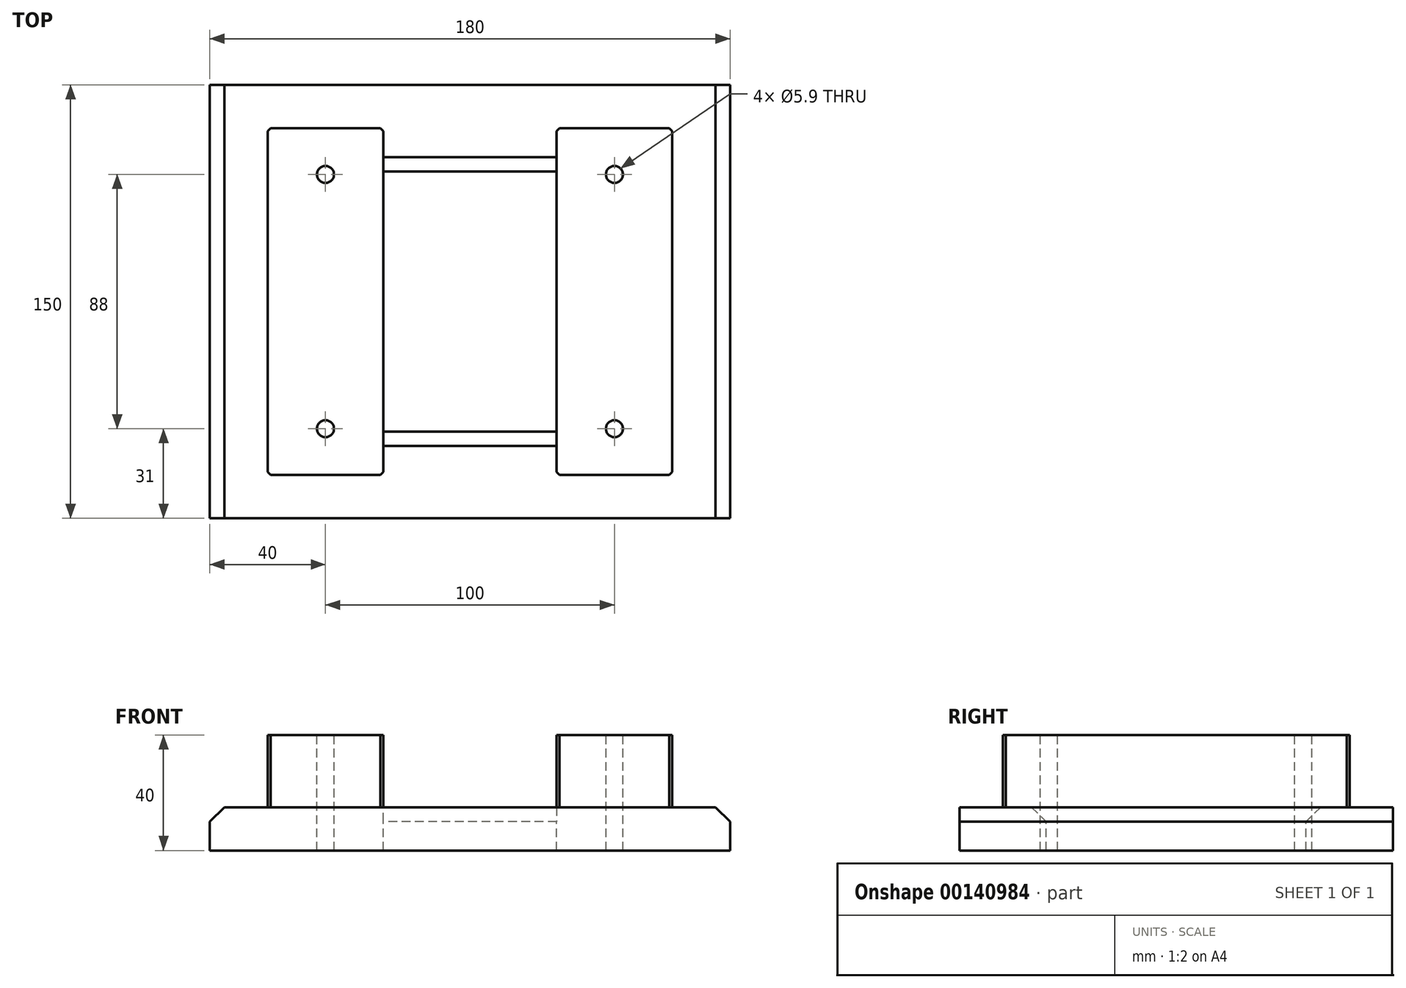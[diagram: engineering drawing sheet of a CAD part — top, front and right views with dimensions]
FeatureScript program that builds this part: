
annotation { "Feature Type Name" : "Feature", "Feature Type Description" : "" }
export const myFeature = defineFeature(function(context is Context, id is Id, definition is map)
    precondition{}
    {
        {
            var Q0;
            Q0=qCreatedBy(makeId("Top.planeOp"),FACE);
            var sketch = newSketch(context, id + "F0", { "sketchPlane" : qUnion([Q0])});
            skLineSegment(sketch, "E0.bottom", {"start": v(90, 75) * mm, "end": v(-90, 75) * mm});
            skLineSegment(sketch, "E0.top", {"start": v(90, -75) * mm, "end": v(-90, -75) * mm});
            skLineSegment(sketch, "E0.left", {"start": v(90, 75) * mm, "end": v(90, -75) * mm});
            skLineSegment(sketch, "E0.right", {"start": v(-90, 75) * mm, "end": v(-90, -75) * mm});
            skPoint(sketch, "E0.middle", {"position": v(0, 0) * mm});
            skLineSegment(sketch, "E1.bottom", {"start": v(30, 45) * mm, "end": v(-30, 45) * mm});
            skLineSegment(sketch, "E1.top", {"start": v(30, -45) * mm, "end": v(-30, -45) * mm});
            skLineSegment(sketch, "E1.left", {"start": v(30, 45) * mm, "end": v(30, -45) * mm});
            skLineSegment(sketch, "E1.right", {"start": v(-30, 45) * mm, "end": v(-30, -45) * mm});
            skLineSegment(sketch, "E2.bottom", {"start": v(50, 44) * mm, "end": v(-50, 44) * mm, "construction": true});
            skLineSegment(sketch, "E2.top", {"start": v(50, -44) * mm, "end": v(-50, -44) * mm, "construction": true});
            skLineSegment(sketch, "E2.left", {"start": v(50, 44) * mm, "end": v(50, -44) * mm, "construction": true});
            skLineSegment(sketch, "E2.right", {"start": v(-50, 44) * mm, "end": v(-50, -44) * mm, "construction": true});
            skCircle(sketch, "E3", {"center": v(-50, 44) * mm, "radius": 2.95 * mm});
            skCircle(sketch, "E4", {"center": v(50, 44) * mm, "radius": 2.95 * mm});
            skCircle(sketch, "E5", {"center": v(50, -44) * mm, "radius": 2.95 * mm});
            skCircle(sketch, "E6", {"center": v(-50, -44) * mm, "radius": 2.95 * mm});
            skLineSegment(sketch, "E7.bottom", {"start": v(-30, 60) * mm, "end": v(-70, 60) * mm});
            skLineSegment(sketch, "E7.top", {"start": v(-30, -60) * mm, "end": v(-70, -60) * mm});
            skLineSegment(sketch, "E7.left", {"start": v(-30, 60) * mm, "end": v(-30, -60) * mm});
            skLineSegment(sketch, "E7.right", {"start": v(-70, 60) * mm, "end": v(-70, -60) * mm});
            skPoint(sketch, "E7.middle", {"position": v(-50, 0) * mm});
            skLineSegment(sketch, "E8.bottom", {"start": v(70, 60) * mm, "end": v(30, 60) * mm});
            skLineSegment(sketch, "E8.top", {"start": v(70, -60) * mm, "end": v(30, -60) * mm});
            skLineSegment(sketch, "E8.left", {"start": v(70, 60) * mm, "end": v(70, -60) * mm});
            skLineSegment(sketch, "E8.right", {"start": v(30, 60) * mm, "end": v(30, -60) * mm});
            skPoint(sketch, "E8.middle", {"position": v(50, 0) * mm});
            skSolve(sketch);
        }
        {
            var Q0;
            Q0=makeQuery(id+"F0.imprint","IMPRINT",FACE,{"disambiguationData":[TD([[makeQuery(id+"F0.imprint","IMPRINT",EDGE,{"derivedFrom":sQuery(id+"F0.wireOp",EDGE,"E0.bottom")}),1.0]])]});
            var Q1;
            Q1=makeQuery(id+"F0.imprint","IMPRINT",FACE,{"disambiguationData":[TD([[makeQuery(id+"F0.imprint","IMPRINT",EDGE,{"derivedFrom":sQuery(id+"F0.wireOp",EDGE,"E3")}),-1.0]])]});
            var Q2;
            Q2=makeQuery(id+"F0.imprint","IMPRINT",FACE,{"disambiguationData":[TD([[makeQuery(id+"F0.imprint","IMPRINT",EDGE,{"derivedFrom":sQuery(id+"F0.wireOp",EDGE,"E4")}),-1.0]])]});
            extrude(context, id + "F1", {"entities" : qUnion([Q0, Q1, Q2]), "oppositeDirection" : true, "depth" : 15 * mm});
        }
        {
            var Q0;
            Q0=makeQuery(id+"F0.imprint","IMPRINT",FACE,{"disambiguationData":[TD([[makeQuery(id+"F0.imprint","IMPRINT",EDGE,{"derivedFrom":sQuery(id+"F0.wireOp",EDGE,"E3")}),-1.0]])]});
            var Q1;
            Q1=makeQuery(id+"F0.imprint","IMPRINT",FACE,{"disambiguationData":[TD([[makeQuery(id+"F0.imprint","IMPRINT",EDGE,{"derivedFrom":sQuery(id+"F0.wireOp",EDGE,"E4")}),-1.0]])]});
            extrude(context, id + "F2", {"entities" : qUnion([Q0, Q1]), "operationType" : NewBodyOperationType.ADD, "depth" : 25 * mm});
        }
        {
            var Q0;
            Q0=makeQuery(id+"F2.opExtrude","SWEPT_EDGE",EDGE,{"disambiguationData":[OSD([sQuery(id+"F0.wireOp",EDGE,"E7.top"),sQuery(id+"F0.wireOp",EDGE,"E7.right")])]});
            var Q1;
            Q1=makeQuery(id+"F2.opExtrude","SWEPT_EDGE",EDGE,{"disambiguationData":[OSD([sQuery(id+"F0.wireOp",EDGE,"E7.top"),sQuery(id+"F0.wireOp",EDGE,"E7.left")])]});
            var Q2;
            Q2=makeQuery(id+"F2.opExtrude","SWEPT_EDGE",EDGE,{"disambiguationData":[OSD([sQuery(id+"F0.wireOp",EDGE,"E8.top"),sQuery(id+"F0.wireOp",EDGE,"E8.right")])]});
            var Q3;
            Q3=makeQuery(id+"F2.opExtrude","SWEPT_EDGE",EDGE,{"disambiguationData":[OSD([sQuery(id+"F0.wireOp",EDGE,"E8.top"),sQuery(id+"F0.wireOp",EDGE,"E8.left")])]});
            var Q4;
            Q4=makeQuery(id+"F2.opExtrude","SWEPT_EDGE",EDGE,{"disambiguationData":[OSD([sQuery(id+"F0.wireOp",EDGE,"E8.bottom"),sQuery(id+"F0.wireOp",EDGE,"E8.left")])]});
            var Q5;
            Q5=makeQuery(id+"F2.opExtrude","SWEPT_EDGE",EDGE,{"disambiguationData":[OSD([sQuery(id+"F0.wireOp",EDGE,"E8.bottom"),sQuery(id+"F0.wireOp",EDGE,"E8.right")])]});
            var Q6;
            Q6=makeQuery(id+"F2.opExtrude","SWEPT_EDGE",EDGE,{"disambiguationData":[OSD([sQuery(id+"F0.wireOp",EDGE,"E7.bottom"),sQuery(id+"F0.wireOp",EDGE,"E7.left")])]});
            var Q7;
            Q7=makeQuery(id+"F2.opExtrude","SWEPT_EDGE",EDGE,{"disambiguationData":[OSD([sQuery(id+"F0.wireOp",EDGE,"E7.bottom"),sQuery(id+"F0.wireOp",EDGE,"E7.right")])]});
            chamfer(context, id + "F3", {"entities" : qUnion([Q0, Q1, Q2, Q3, Q4, Q5, Q6, Q7]), "width" : 1 * mm, "tangentPropagation" : true});
        }
        {
            var Q0;
            Q0=makeQuery(id+"F1.opExtrude","CAP_EDGE",EDGE,{"disambiguationData":[OSD([sQuery(id+"F0.wireOp",EDGE,"E1.bottom")])],"isStart":true});
            var Q1;
            Q1=makeQuery(id+"F1.opExtrude","CAP_EDGE",EDGE,{"disambiguationData":[OSD([sQuery(id+"F0.wireOp",EDGE,"E1.top")])],"isStart":true});
            var Q2;
            Q2=makeQuery(id+"F1.opExtrude","CAP_EDGE",EDGE,{"disambiguationData":[OSD([sQuery(id+"F0.wireOp",EDGE,"E0.right")])],"isStart":true});
            var Q3;
            Q3=makeQuery(id+"F1.opExtrude","CAP_EDGE",EDGE,{"disambiguationData":[OSD([sQuery(id+"F0.wireOp",EDGE,"E0.left")])],"isStart":true});
            chamfer(context, id + "F4", {"entities" : qUnion([Q0, Q1, Q2, Q3]), "width" : 5 * mm, "tangentPropagation" : true});
        }
    });
